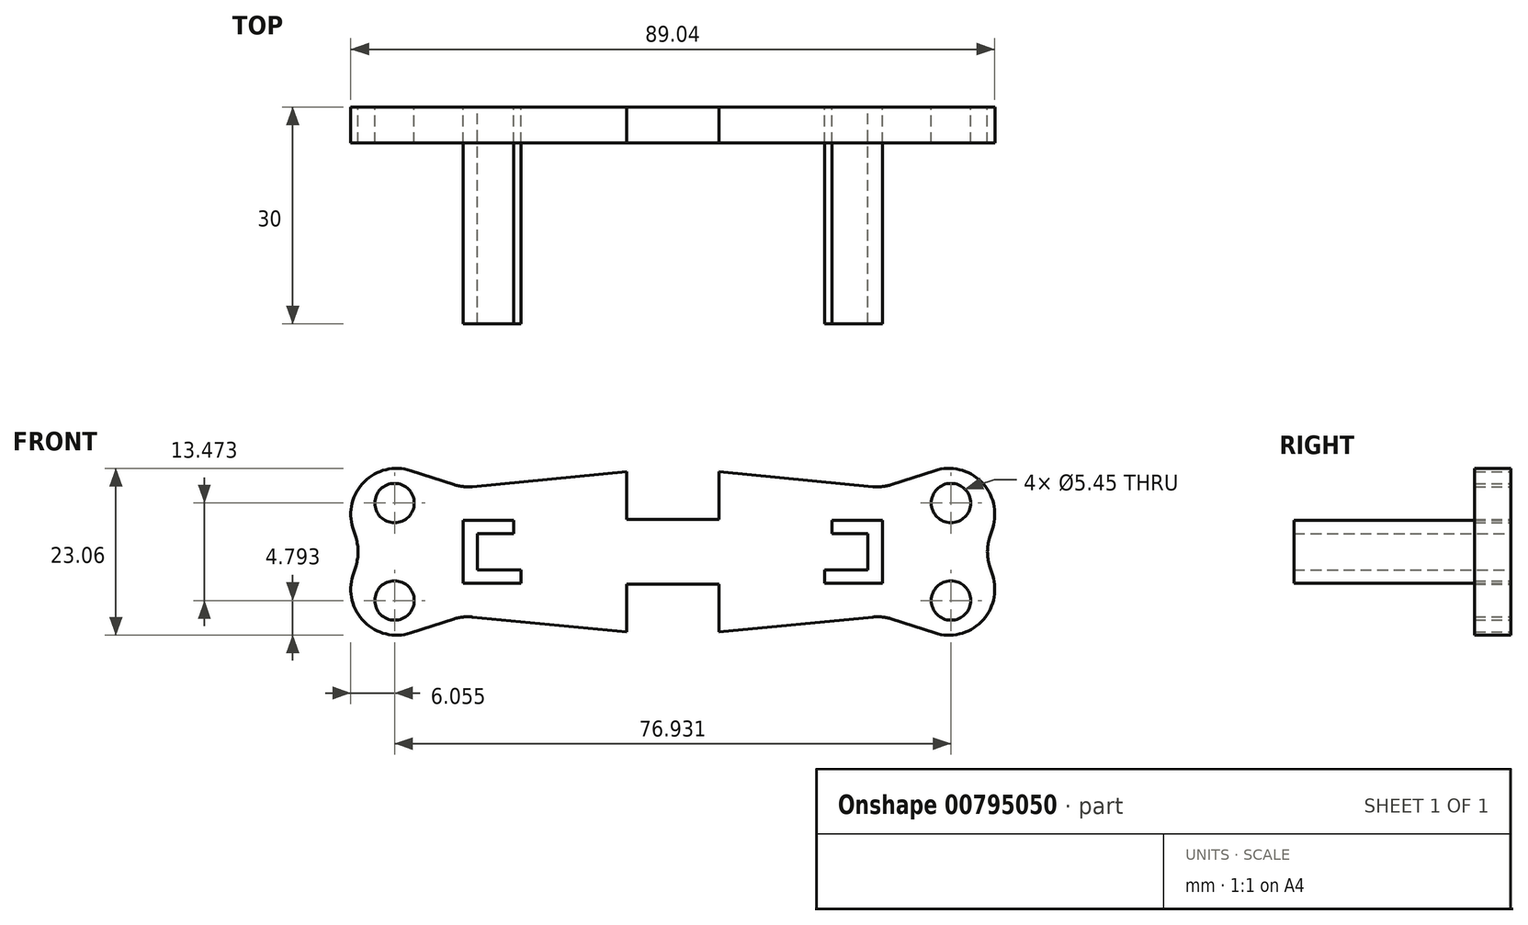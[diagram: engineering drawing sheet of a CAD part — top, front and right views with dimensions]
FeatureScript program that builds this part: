
annotation { "Feature Type Name" : "Feature", "Feature Type Description" : "" }
export const myFeature = defineFeature(function(context is Context, id is Id, definition is map)
    precondition{}
    {
        {
            var Q0;
            Q0=qCreatedBy(makeId("Front.planeOp"),FACE);
            var sketch = newSketch(context, id + "F0", { "sketchPlane" : qUnion([Q0])});
            skLineSegment(sketch, "E0", {"start": v(29, -4.37) * mm, "end": v(29, 0) * mm});
            skPoint(sketch, "E1", {"position": v(0, 0) * mm});
            skLineSegment(sketch, "E2", {"start": v(27, 0) * mm, "end": v(27, -2.5) * mm});
            skLineSegment(sketch, "E3", {"start": v(27, -2.5) * mm, "end": v(21, -2.5) * mm});
            skLineSegment(sketch, "E4", {"start": v(21, -2.5) * mm, "end": v(21, -4.38) * mm});
            skLineSegment(sketch, "E5", {"start": v(21, -4.38) * mm, "end": v(29, -4.37) * mm});
            skLineSegment(sketch, "E6.MirrorCS", {"start": v(29, 4.37) * mm, "end": v(29, 0) * mm});
            skLineSegment(sketch, "E7.MirrorCS", {"start": v(21, 4.37) * mm, "end": v(29, 4.37) * mm});
            skLineSegment(sketch, "E8.MirrorCS", {"start": v(22, 2.5) * mm, "end": v(22, 4.37) * mm});
            skLineSegment(sketch, "E9.MirrorCS", {"start": v(27, 2.5) * mm, "end": v(22, 2.5) * mm});
            skLineSegment(sketch, "E10.MirrorCS", {"start": v(27, 0) * mm, "end": v(27, 2.5) * mm});
            skLineSegment(sketch, "E11", {"start": v(26, 0) * mm, "end": v(28, 0) * mm});
            skLineSegment(sketch, "E12", {"start": v(27, 0) * mm, "end": v(29, 0) * mm});
            skLineSegment(sketch, "E13.MirrorCS", {"start": v(-26, 0) * mm, "end": v(-28, 0) * mm});
            skLineSegment(sketch, "E14.MirrorCS", {"start": v(-27, 0) * mm, "end": v(-29, 0) * mm});
            skLineSegment(sketch, "E15.MirrorCS", {"start": v(-27, 0) * mm, "end": v(-27, -2.5) * mm});
            skLineSegment(sketch, "E16.MirrorCS", {"start": v(-21, -2.5) * mm, "end": v(-21, -4.38) * mm});
            skLineSegment(sketch, "E17.MirrorCS", {"start": v(-27, 0) * mm, "end": v(-27, 2.5) * mm});
            skLineSegment(sketch, "E18.MirrorCS", {"start": v(-29, -4.37) * mm, "end": v(-29, 0) * mm});
            skLineSegment(sketch, "E19.MirrorCS", {"start": v(-22, 2.5) * mm, "end": v(-22, 4.37) * mm});
            skLineSegment(sketch, "E20.MirrorCS", {"start": v(-21, 4.37) * mm, "end": v(-29, 4.37) * mm});
            skLineSegment(sketch, "E21.MirrorCS", {"start": v(-27, 2.5) * mm, "end": v(-22, 2.5) * mm});
            skLineSegment(sketch, "E22.MirrorCS", {"start": v(-21, -4.38) * mm, "end": v(-29, -4.37) * mm});
            skLineSegment(sketch, "E23.MirrorCS", {"start": v(-29, 4.37) * mm, "end": v(-29, 0) * mm});
            skLineSegment(sketch, "E24.MirrorCS", {"start": v(-27, -2.5) * mm, "end": v(-21, -2.5) * mm});
            skSolve(sketch);
        }
        {
            var Q0;
            Q0=qCreatedBy(makeId("Front.planeOp"),FACE);
            var sketch = newSketch(context, id + "F1", { "sketchPlane" : qUnion([Q0])});
            skPoint(sketch, "E25", {"position": v(0, 0) * mm});
            skPoint(sketch, "E25.positionSnap0", {"position": v(29, 0) * mm});
            skPoint(sketch, "E25.positionSnap1", {"position": v(0, 15) * mm});
            skLineSegment(sketch, "E26", {"start": v(29, 8.9) * mm, "end": v(29, -8.9) * mm});
            skLineSegment(sketch, "E27", {"start": v(-29, -8.9) * mm, "end": v(-29, 8.9) * mm});
            skLineSegment(sketch, "E28", {"start": v(29, -8.9) * mm, "end": v(6.4, -11.05) * mm});
            skLineSegment(sketch, "E29", {"start": v(-38.02, -8.9) * mm, "end": v(-38.02, 0) * mm});
            skLineSegment(sketch, "E30", {"start": v(6.4, -11.05) * mm, "end": v(6.4, -4.45) * mm});
            skPoint(sketch, "E30.endSnap0", {"position": v(-38.02, -4.45) * mm});
            skLineSegment(sketch, "E31", {"start": v(6.4, -4.45) * mm, "end": v(0, -4.45) * mm});
            skLineSegment(sketch, "E32.MirrorCS", {"start": v(-6.4, -11.05) * mm, "end": v(-6.4, -4.45) * mm});
            skLineSegment(sketch, "E33.MirrorCS", {"start": v(-6.4, -4.45) * mm, "end": v(0, -4.45) * mm});
            skLineSegment(sketch, "E34.MirrorCS", {"start": v(-29, -8.9) * mm, "end": v(-6.4, -11.05) * mm});
            skLineSegment(sketch, "E35.MirrorCS", {"start": v(-29, 8.9) * mm, "end": v(-6.4, 11.05) * mm});
            skLineSegment(sketch, "E36.MirrorCS", {"start": v(-6.4, 11.05) * mm, "end": v(-6.4, 4.45) * mm});
            skLineSegment(sketch, "E37.MirrorCS", {"start": v(-6.4, 4.45) * mm, "end": v(0, 4.45) * mm});
            skLineSegment(sketch, "E38.MirrorCS", {"start": v(6.4, 4.45) * mm, "end": v(0, 4.45) * mm});
            skLineSegment(sketch, "E39.MirrorCS", {"start": v(6.4, 11.05) * mm, "end": v(6.4, 4.45) * mm});
            skLineSegment(sketch, "E40.MirrorCS", {"start": v(29, 8.9) * mm, "end": v(6.4, 11.05) * mm});
            skSolve(sketch);
        }
        {
            var Q0;
            Q0 = qSketchRegion(id + "F0", true);
            extrude(context, id + "F2", {"entities" : qUnion([Q0]), "depth" : 30 * mm, "offsetDistance" : 25.4 * mm});
        }
        {
            var Q0;
            Q0 = qSketchRegion(id + "F1", true);
            extrude(context, id + "F3", {"entities" : qUnion([Q0]), "depth" : 5 * mm, "offsetDistance" : 25.4 * mm});
        }
        {
            var Q0;
            Q0=makeQuery(id+"F3.opExtrude","CAP_FACE",FACE,{"disambiguationData":[OSD([sQuery(id+"F1.wireOp",EDGE,"VLsbzq37-3D8D-qg34-oOXw-Vgue8LgEdkqq"),sQuery(id+"F1.wireOp",EDGE,"0IUa2fHP-s64G-SHAU-VyQA-nZvo7XuSEz9r"),sQuery(id+"F1.wireOp",EDGE,"611c17cf-ed80-4548-8a0f-41c9b028268c0.MirrorCS"),sQuery(id+"F1.wireOp",EDGE,"e3e70f21-3547-4834-9a51-a8a6651e2a050.MirrorCS"),sQuery(id+"F1.wireOp",EDGE,"b28a3862-f930-4a78-9749-6ba2aa7eee2e0.MirrorCS"),sQuery(id+"F1.wireOp",EDGE,"52579144-dd8c-45e6-a782-5b9c21cd64b00.MirrorCS"),sQuery(id+"F1.wireOp",EDGE,"9fda6fa9-e149-4163-bbdf-9c0a3d88ba190.MirrorCS"),sQuery(id+"F1.wireOp",EDGE,"aa9dab99-4663-4797-a324-3fa35b7749050.MirrorCS"),sQuery(id+"F1.wireOp",EDGE,"E26"),sQuery(id+"F1.wireOp",EDGE,"E27")])],"isStart":true});
            var sketch = newSketch(context, id + "F4", { "sketchPlane" : qUnion([Q0])});
            skLineSegment(sketch, "E41", {"start": v(-29, 8.9) * mm, "end": v(-47.93, 15) * mm});
            skLineSegment(sketch, "E42", {"start": v(-47.93, 15) * mm, "end": v(-38.47, 11.95) * mm});
            skLineSegment(sketch, "E43", {"start": v(-47.93, 15) * mm, "end": v(-43.2, 0) * mm});
            skPoint(sketch, "E43.endSnap0", {"position": v(-43.2, 13.47) * mm});
            skLineSegment(sketch, "E44.MirrorCS", {"start": v(-47.93, -15) * mm, "end": v(-43.2, 0) * mm});
            skLineSegment(sketch, "E45.MirrorCS", {"start": v(-47.93, -15) * mm, "end": v(-38.47, -11.95) * mm});
            skLineSegment(sketch, "E46.MirrorCS", {"start": v(-29, -8.9) * mm, "end": v(-47.93, -15) * mm});
            skLineSegment(sketch, "E47.MirrorCS", {"start": v(47.93, 15) * mm, "end": v(38.47, 11.95) * mm});
            skLineSegment(sketch, "E48.MirrorCS", {"start": v(29, 8.9) * mm, "end": v(47.93, 15) * mm});
            skLineSegment(sketch, "E49.MirrorCS", {"start": v(47.93, 15) * mm, "end": v(43.2, 0) * mm});
            skLineSegment(sketch, "E50.MirrorCS", {"start": v(47.93, -15) * mm, "end": v(43.2, 0) * mm});
            skLineSegment(sketch, "E51.MirrorCS", {"start": v(29, -8.9) * mm, "end": v(47.93, -15) * mm});
            skLineSegment(sketch, "E52", {"start": v(-43.2, 13.47) * mm, "end": v(-43.2, 0) * mm, "construction": true});
            skCircle(sketch, "E53", {"center": v(-38.47, 6.74) * mm, "radius": 2.72 * mm});
            skPoint(sketch, "E53.centerSnap0", {"position": v(-43.2, 6.74) * mm});
            skCircle(sketch, "E54.MirrorC", {"center": v(-38.47, -6.74) * mm, "radius": 2.72 * mm});
            skCircle(sketch, "E55.MirrorC", {"center": v(38.47, 6.74) * mm, "radius": 2.72 * mm});
            skCircle(sketch, "E56.MirrorC", {"center": v(38.47, -6.74) * mm, "radius": 2.72 * mm});
            skSolve(sketch);
        }
        {
            var Q0;
            Q0=makeQuery(id+"F4.imprint","IMPRINT",FACE,{"disambiguationData":[TD([[makeQuery(id+"F4.imprint","IMPRINT",EDGE,{"derivedFrom":sQuery(id+"F4.wireOp",EDGE,"E41")}),1.0]])]});
            var Q1;
            {var subQ0=sQuery(id+"F4.wireOp",EDGE,"E49.MirrorCS");Q1=makeQuery(id+"F4.imprint","IMPRINT",FACE,{"disambiguationData":[TD([[makeQuery(id+"F4.imprint","IMPRINT",EDGE,{"derivedFrom":subQ0}),-1.0]])]});}
            extrude(context, id + "F5", {"entities" : qUnion([Q0, Q1]), "operationType" : NewBodyOperationType.ADD, "oppositeDirection" : true, "depth" : 5 * mm, "offsetDistance" : 25.4 * mm});
        }
        {
            var Q0;
            Q0=makeQuery(id+"F5.opExtrude","SWEPT_EDGE",EDGE,{"disambiguationData":[OSD([sQuery(id+"F4.wireOp",EDGE,"E43"),sQuery(id+"F4.wireOp",EDGE,"E44.MirrorCS")])]});
            var Q1;
            Q1=makeQuery(id+"F5.opExtrude","SWEPT_EDGE",EDGE,{"disambiguationData":[OSD([sQuery(id+"F4.wireOp",EDGE,"E42"),sQuery(id+"F4.wireOp",EDGE,"E43")])]});
            var Q2;
            Q2=makeQuery(id+"F5.opExtrude","SWEPT_EDGE",EDGE,{"disambiguationData":[OSD([sQuery(id+"F4.wireOp",EDGE,"E44.MirrorCS"),sQuery(id+"F4.wireOp",EDGE,"E46.MirrorCS")])]});
            var Q3;
            {var subQ0=sQuery(id+"F1.wireOp",EDGE,"E26");var subQ1=sQuery(id+"F1.wireOp",EDGE,"52579144-dd8c-45e6-a782-5b9c21cd64b00.MirrorCS");Q3=makeQuery(id+"F5.boolean.opBoolean","MERGE",EDGE,{"derivedFrom":[makeQuery(id+"F3.opExtrude","SWEPT_EDGE",EDGE,{"disambiguationData":[OSD([subQ1,subQ0])]}),makeQuery(id+"F5.opExtrude","SWEPT_EDGE",EDGE,{"disambiguationData":[OSD([subQ1,subQ0,sQuery(id+"F4.wireOp",EDGE,"E46.MirrorCS")])]})]});}
            var Q4;
            Q4=makeQuery(id+"F3.opExtrude","SWEPT_EDGE",EDGE,{"disambiguationData":[OSD([sQuery(id+"F1.wireOp",EDGE,"b28a3862-f930-4a78-9749-6ba2aa7eee2e0.MirrorCS"),sQuery(id+"F1.wireOp",EDGE,"52579144-dd8c-45e6-a782-5b9c21cd64b00.MirrorCS")])]});
            var Q5;
            Q5=makeQuery(id+"F3.opExtrude","SWEPT_EDGE",EDGE,{"disambiguationData":[OSD([sQuery(id+"F1.wireOp",EDGE,"b28a3862-f930-4a78-9749-6ba2aa7eee2e0.MirrorCS"),sQuery(id+"F1.wireOp",EDGE,"9fda6fa9-e149-4163-bbdf-9c0a3d88ba190.MirrorCS")])]});
            var Q6;
            Q6=makeQuery(id+"F3.opExtrude","SWEPT_EDGE",EDGE,{"disambiguationData":[OSD([sQuery(id+"F1.wireOp",EDGE,"9fda6fa9-e149-4163-bbdf-9c0a3d88ba190.MirrorCS"),sQuery(id+"F1.wireOp",EDGE,"aa9dab99-4663-4797-a324-3fa35b7749050.MirrorCS")])]});
            var Q7;
            {var subQ0=sQuery(id+"F1.wireOp",EDGE,"E27");var subQ1=sQuery(id+"F1.wireOp",EDGE,"aa9dab99-4663-4797-a324-3fa35b7749050.MirrorCS");Q7=makeQuery(id+"F5.boolean.opBoolean","MERGE",EDGE,{"derivedFrom":[makeQuery(id+"F3.opExtrude","SWEPT_EDGE",EDGE,{"disambiguationData":[OSD([subQ1,subQ0])]}),makeQuery(id+"F5.opExtrude","SWEPT_EDGE",EDGE,{"disambiguationData":[OSD([subQ1,subQ0,sQuery(id+"F4.wireOp",EDGE,"E51.MirrorCS")])]})]});}
            var Q8;
            Q8=makeQuery(id+"F5.opExtrude","SWEPT_EDGE",EDGE,{"disambiguationData":[OSD([sQuery(id+"F4.wireOp",EDGE,"E50.MirrorCS"),sQuery(id+"F4.wireOp",EDGE,"E51.MirrorCS")])]});
            var Q9;
            Q9=makeQuery(id+"F5.opExtrude","SWEPT_EDGE",EDGE,{"disambiguationData":[OSD([sQuery(id+"F4.wireOp",EDGE,"E49.MirrorCS"),sQuery(id+"F4.wireOp",EDGE,"E50.MirrorCS")])]});
            var Q10;
            Q10=makeQuery(id+"F5.opExtrude","SWEPT_EDGE",EDGE,{"disambiguationData":[OSD([sQuery(id+"F4.wireOp",EDGE,"E48.MirrorCS"),sQuery(id+"F4.wireOp",EDGE,"E49.MirrorCS")])]});
            var Q11;
            {var subQ0=sQuery(id+"F1.wireOp",EDGE,"E27");var subQ1=sQuery(id+"F1.wireOp",EDGE,"VLsbzq37-3D8D-qg34-oOXw-Vgue8LgEdkqq");Q11=makeQuery(id+"F5.boolean.opBoolean","MERGE",EDGE,{"derivedFrom":[makeQuery(id+"F3.opExtrude","SWEPT_EDGE",EDGE,{"disambiguationData":[OSD([subQ1,subQ0])]}),makeQuery(id+"F5.opExtrude","SWEPT_EDGE",EDGE,{"disambiguationData":[OSD([subQ1,subQ0,sQuery(id+"F4.wireOp",EDGE,"E48.MirrorCS")])]})]});}
            var Q12;
            Q12=makeQuery(id+"F3.opExtrude","SWEPT_EDGE",EDGE,{"disambiguationData":[OSD([sQuery(id+"F1.wireOp",EDGE,"VLsbzq37-3D8D-qg34-oOXw-Vgue8LgEdkqq"),sQuery(id+"F1.wireOp",EDGE,"0IUa2fHP-s64G-SHAU-VyQA-nZvo7XuSEz9r")])]});
            var Q13;
            Q13=makeQuery(id+"F3.opExtrude","SWEPT_EDGE",EDGE,{"disambiguationData":[OSD([sQuery(id+"F1.wireOp",EDGE,"0IUa2fHP-s64G-SHAU-VyQA-nZvo7XuSEz9r"),sQuery(id+"F1.wireOp",EDGE,"611c17cf-ed80-4548-8a0f-41c9b028268c0.MirrorCS")])]});
            var Q14;
            Q14=makeQuery(id+"F3.opExtrude","SWEPT_EDGE",EDGE,{"disambiguationData":[OSD([sQuery(id+"F1.wireOp",EDGE,"611c17cf-ed80-4548-8a0f-41c9b028268c0.MirrorCS"),sQuery(id+"F1.wireOp",EDGE,"e3e70f21-3547-4834-9a51-a8a6651e2a050.MirrorCS")])]});
            var Q15;
            {var subQ0=sQuery(id+"F1.wireOp",EDGE,"E26");var subQ1=sQuery(id+"F1.wireOp",EDGE,"e3e70f21-3547-4834-9a51-a8a6651e2a050.MirrorCS");Q15=makeQuery(id+"F5.boolean.opBoolean","MERGE",EDGE,{"derivedFrom":[makeQuery(id+"F3.opExtrude","SWEPT_EDGE",EDGE,{"disambiguationData":[OSD([subQ1,subQ0])]}),makeQuery(id+"F5.opExtrude","SWEPT_EDGE",EDGE,{"disambiguationData":[OSD([subQ1,subQ0,sQuery(id+"F4.wireOp",EDGE,"E41")])]})]});}
            fillet(context, id + "F6", {"entities" : qUnion([Q0, Q1, Q2, Q3, Q4, Q5, Q6, Q7, Q8, Q9, Q10, Q11, Q12, Q13, Q14, Q15]), "radius" : 6.35 * mm, "tangentPropagation" : true, "allowEdgeOverflow" : false});
        }
    });
